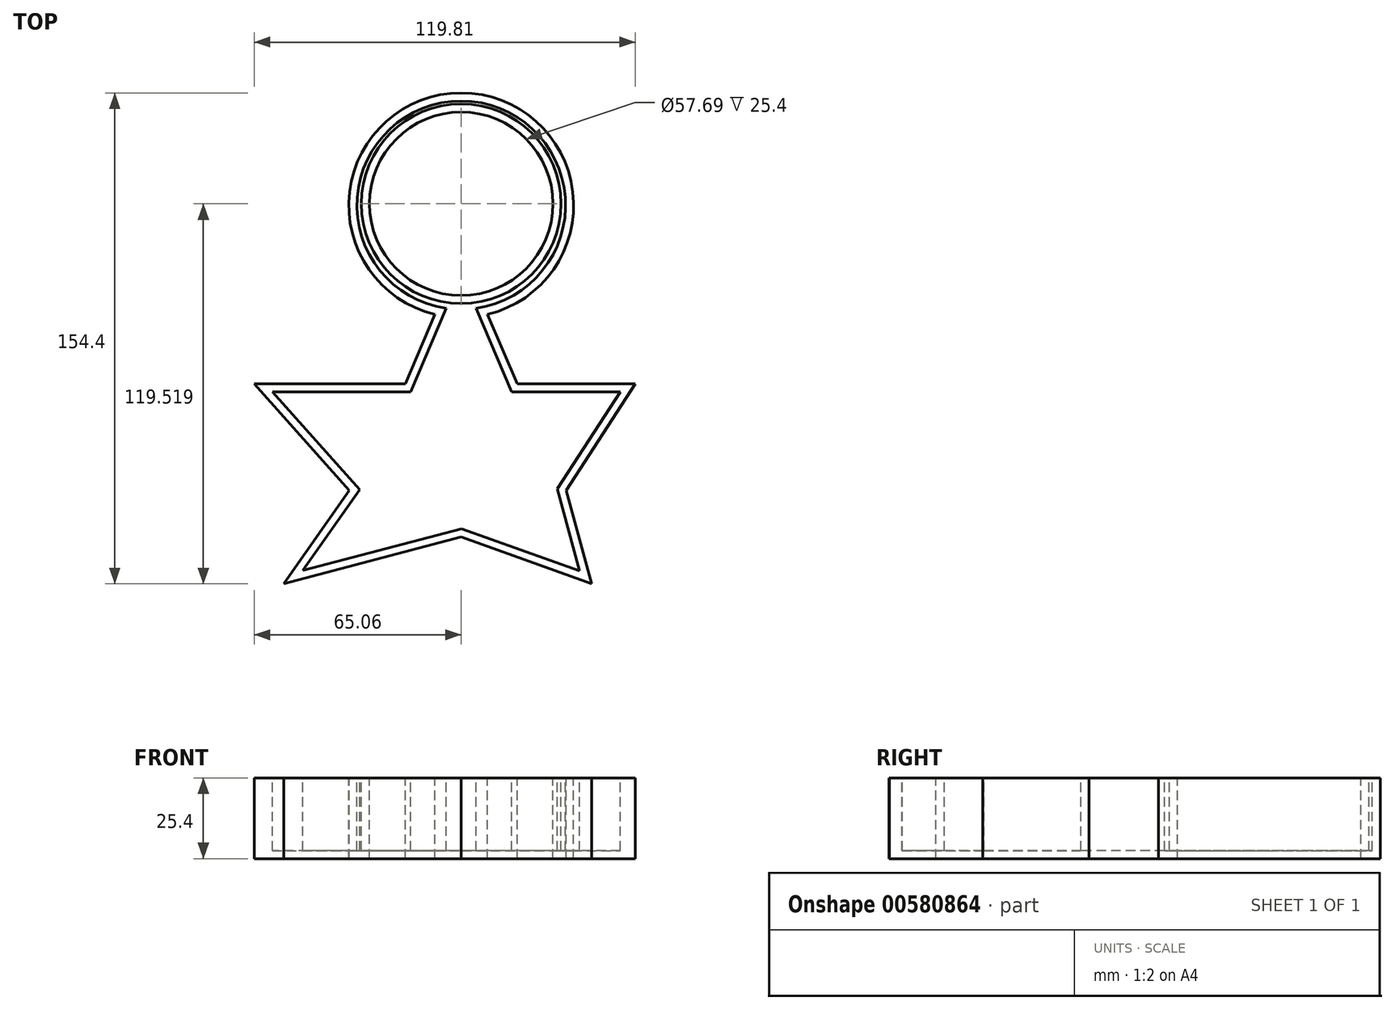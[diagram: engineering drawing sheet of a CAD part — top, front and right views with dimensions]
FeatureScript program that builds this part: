
annotation { "Feature Type Name" : "Feature", "Feature Type Description" : "" }
export const myFeature = defineFeature(function(context is Context, id is Id, definition is map)
    precondition{}
    {
        {
            var Q0;
            Q0=qCreatedBy(makeId("Top.planeOp"),FACE);
            var sketch = newSketch(context, id + "F0", { "sketchPlane" : qUnion([Q0])});
            skLineSegment(sketch, "E0", {"start": v(0, 45.23) * mm, "end": v(-17.56, 3.97) * mm});
            skLineSegment(sketch, "E1", {"start": v(-17.56, 3.97) * mm, "end": v(-65.06, 3.97) * mm});
            skLineSegment(sketch, "E2", {"start": v(-65.06, 3.97) * mm, "end": v(-35.18, -29.54) * mm});
            skLineSegment(sketch, "E3", {"start": v(-35.18, -29.54) * mm, "end": v(-55.83, -58.95) * mm});
            skLineSegment(sketch, "E4", {"start": v(-55.83, -58.95) * mm, "end": v(0, -44.24) * mm});
            skLineSegment(sketch, "E5", {"start": v(0, -44.24) * mm, "end": v(41.15, -58.95) * mm});
            skLineSegment(sketch, "E6", {"start": v(41.15, -59.57) * mm, "end": v(33.01, -29.54) * mm});
            skLineSegment(sketch, "E7", {"start": v(33.01, -29.54) * mm, "end": v(54.75, 3.97) * mm});
            skLineSegment(sketch, "E8", {"start": v(54.75, 3.97) * mm, "end": v(17.58, 3.97) * mm});
            skLineSegment(sketch, "E9", {"start": v(0, 45.23) * mm, "end": v(17.58, 3.97) * mm});
            skSolve(sketch);
        }
        {
            var Q0;
            Q0 = qSketchRegion(id + "F0", true);
            extrude(context, id + "F1", {"entities" : qUnion([Q0]), "oppositeDirection" : true, "depth" : 25.4 * mm, "offsetDistance" : 25.4 * mm});
        }
        {
            var Q0;
            Q0=qCreatedBy(makeId("Top.planeOp"),FACE);
            var sketch = newSketch(context, id + "F2", { "sketchPlane" : qUnion([Q0])});
            skCircle(sketch, "E10", {"center": v(0, 60.12) * mm, "radius": 35.33 * mm});
            skSolve(sketch);
        }
        {
            var Q0;
            Q0 = qSketchRegion(id + "F2", true);
            extrude(context, id + "F3", {"entities" : qUnion([Q0]), "operationType" : NewBodyOperationType.ADD, "depth" : -25.4 * mm, "offsetDistance" : 25.4 * mm});
        }
        {
            var Q0;
            Q0=qCreatedBy(makeId("Top.planeOp"),FACE);
            var sketch = newSketch(context, id + "F4", { "sketchPlane" : qUnion([Q0])});
            skCircle(sketch, "E11", {"center": v(0, 60.57) * mm, "radius": 28.85 * mm});
            skSolve(sketch);
        }
        {
            var Q0;
            Q0=makeQuery(id+"F4.imprint","IMPRINT",FACE,{"disambiguationData":[TD([[makeQuery(id+"F4.imprint","IMPRINT",EDGE,{"derivedFrom":sQuery(id+"F4.wireOp",EDGE,"E11")}),1.0]])]});
            extrude(context, id + "F5", {"entities" : qUnion([Q0]), "operationType" : NewBodyOperationType.REMOVE, "oppositeDirection" : true, "depth" : 127 * mm, "offsetDistance" : 25.4 * mm});
        }
        {
            var Q0;
            Q0=makeQuery(id+"F3.boolean.opBoolean","MERGE",FACE,{"derivedFrom":[makeQuery(id+"F1.opExtrude","CAP_FACE",FACE,{"disambiguationData":[OSD([sQuery(id+"F0.wireOp",EDGE,"E0"),sQuery(id+"F0.wireOp",EDGE,"E1"),sQuery(id+"F0.wireOp",EDGE,"E2"),sQuery(id+"F0.wireOp",EDGE,"E3"),sQuery(id+"F0.wireOp",EDGE,"E4"),sQuery(id+"F0.wireOp",EDGE,"E5"),sQuery(id+"F0.wireOp",EDGE,"E6"),sQuery(id+"F0.wireOp",EDGE,"E7"),sQuery(id+"F0.wireOp",EDGE,"E8"),sQuery(id+"F0.wireOp",EDGE,"E9")])],"isStart":true}),makeQuery(id+"F3.opExtrude","CAP_FACE",FACE,{"disambiguationData":[OSD([sQuery(id+"F2.wireOp",EDGE,"E10")])],"isStart":true})]});
            shell(context, id + "F6", {"entities" : qUnion([Q0]), "thickness" : 2.54 * mm});
        }
    });
